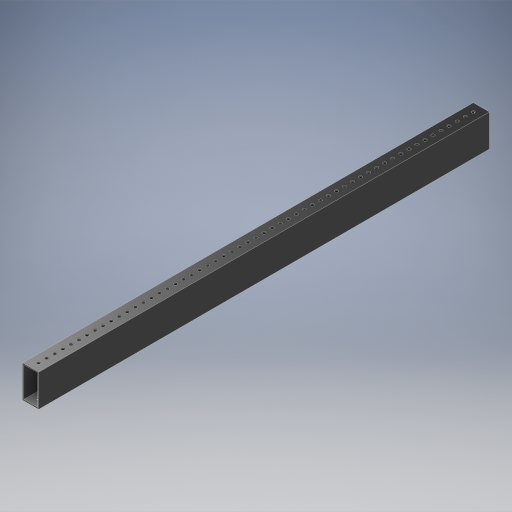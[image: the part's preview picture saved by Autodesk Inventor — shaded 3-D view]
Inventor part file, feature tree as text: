
AUTODESK INVENTOR PART (.ipt)
format: ipt  version: 2024.2 (Build 282272000, 272)  size: 816,640 bytes
history: native  units: in
note: dims shown in document units (in); Inventor stores cm internally (conversion verified against a paired STEP export)
features: other x13, extrude x10, hole x3, pattern_linear x3, mirror x3, sheet_metal_op x1, plane x1, sketch x1
ambient origin geometry x8: Origin, YZ Plane, XZ Plane, XY Plane, X Axis, Y Axis, Z Axis, Center Point
bodies: Solid1 (feature_tree)
feature tree (35):
  other  "Blocks"
  other  "Base Sketch"
  extrude  "Base"  Depth=1.0in
  extrude  "MAX Corner"  Depth=0.0625in
  extrude  "MAX Corner Cut"  Depth=0.0625in
  extrude  "Scribe Lines"  Depth=1.0in
  other  "Side Middle"
  other  "Top Middle"
  other  "Side Holes Sketch"
  hole  "Top Side Hole"  [1 undecoded]
  hole  "Mid Side Hole"  [1 undecoded]
  hole  "Btm Side Hole"  [1 undecoded]
  pattern_linear  "Side Holes"  Spacing1=0.04in  [1 undecoded]
  mirror  "Side Mirror"
  extrude  "MAXTube Hole"  Depth=28.0in
  extrude  "MAXTube Outside"  TaperAngle=0.0deg  [1 undecoded]
  pattern_linear  "MAXTube Pattern"  Spacing1=28.0in  [1 undecoded]
  mirror  "MAXTube Mirror"
  extrude  "Left Top Hole"  TaperAngle=0.0deg  [1 undecoded]
  extrude  "Mid Top Hole"  TaperAngle=0.0deg  [1 undecoded]
  extrude  "Right Top Hole"  Depth=1.0in
  pattern_linear  "Top Holes"  Spacing1=0.0in  [1 undecoded]
  mirror  "Top Mirror"
  extrude  "Extrusion11"  Depth=1.0in
  sheet_metal_op  "Corner"
  other  "MAXTube"
  plane  "Work Plane3"
  sketch  "Sketch5"  dims[d0=2.0in d1=1.0in d2=0.0625in d3=0.0625in d4=0.4375in d5=0.04in d6=0.0671in d7=0.0272in d8=0.0in d9=0.0in d10=0.0in d11=0.085in d12=0.085in d16=0.04in d17=0.04in d18=0.04in d19=0.04in d20=28.0in d21=0.0in d22=28.0in d23=0.0in d24=0.0in d25=0.0in d26=0.005in d30=0.0in d31=0.0in d34=0.5in d35=0.5in d38=0.5in d40=0.196in d41=0.75in d42=0.375in d43=0.25in d44=0.5635in d45=1.0in d46=0.8108in d47=0.196in d48=0.75in d49=0.375in d50=0.25in d51=0.5635in d52=1.0in d53=0.8108in d54=0.196in d55=0.75in d56=0.375in d57=0.25in d58=0.5635in d59=1.0in d60=0.8108in d61=0.5in d62=0.3937in d64=0.5in d69=1.5in d70=0.0in d71=0.0in d72=3.1496in d74=2.0in d78=2.0in d79=-14.0in d80=0.196in d81=0.0in d82=0.0in d83=0.5in d84=0.0in d85=0.0in d86=0.0in d87=0.0in d88=0.0in d89=0.0in d90=11.0236in d92=0.5in d93=1.0in d95=0.0in d96=0.0in d97=0.5in d98=26.0in d100=-14.0in d101=0.25in d102=0.25in d103=0.25in d104=0.25in d105=0.25in d106=0.25in d107=0.25in d108=0.25in d109=0.5in d110=0.0in]
  other  "Corner:5"
  other  "Corner:6"
  other  "Corner:7"
  other  "Corner:8"
  other  "MAXTube:1"
  other  "MAXTube:2"
  other  "MAXTube:3"
note: 9 required parameter values undecoded (feature->parameter linkage not recoverable at this tier; creation-order binding heuristic only, values carry confidence <= 0.55)
